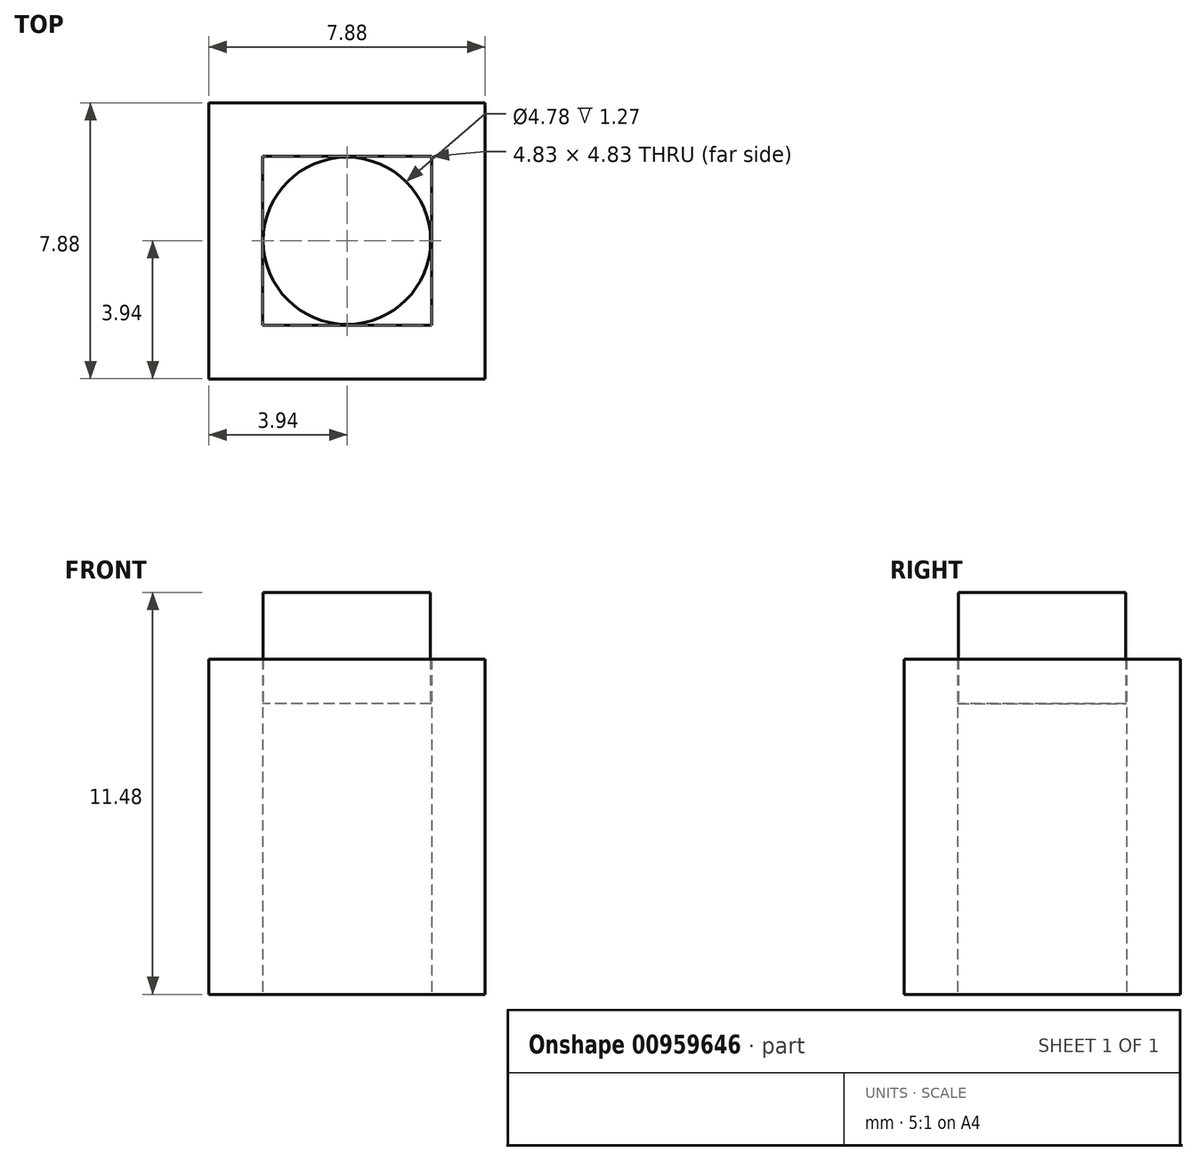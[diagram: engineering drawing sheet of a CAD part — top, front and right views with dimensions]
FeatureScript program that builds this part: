
annotation { "Feature Type Name" : "Feature", "Feature Type Description" : "" }
export const myFeature = defineFeature(function(context is Context, id is Id, definition is map)
    precondition{}
    {
        {
            var Q0;
            Q0=qCreatedBy(makeId("Top.planeOp"),FACE);
            var sketch = newSketch(context, id + "F0", { "sketchPlane" : qUnion([Q0])});
            skLineSegment(sketch, "E0.bottom", {"start": v(2.41, 2.41) * mm, "end": v(-2.41, 2.41) * mm});
            skLineSegment(sketch, "E0.top", {"start": v(2.41, -2.41) * mm, "end": v(-2.41, -2.41) * mm});
            skLineSegment(sketch, "E0.left", {"start": v(2.41, 2.41) * mm, "end": v(2.41, -2.41) * mm});
            skLineSegment(sketch, "E0.right", {"start": v(-2.41, 2.41) * mm, "end": v(-2.41, -2.41) * mm});
            skPoint(sketch, "E0.middle", {"position": v(0, 0) * mm});
            skLineSegment(sketch, "E1.bottom", {"start": v(3.94, 3.94) * mm, "end": v(-3.94, 3.94) * mm});
            skLineSegment(sketch, "E1.top", {"start": v(3.94, -3.94) * mm, "end": v(-3.94, -3.94) * mm});
            skLineSegment(sketch, "E1.left", {"start": v(3.94, 3.94) * mm, "end": v(3.94, -3.94) * mm});
            skLineSegment(sketch, "E1.right", {"start": v(-3.94, 3.94) * mm, "end": v(-3.94, -3.94) * mm});
            skCircle(sketch, "E2", {"center": v(0, 0) * mm, "radius": 2.39 * mm});
            skSolve(sketch);
        }
        {
            var Q0;
            Q0=makeQuery(id+"F0.imprint","IMPRINT",FACE,{"disambiguationData":[TD([[makeQuery(id+"F0.imprint","IMPRINT",EDGE,{"derivedFrom":sQuery(id+"F0.wireOp",EDGE,"E0.bottom")}),-1.0]])]});
            extrude(context, id + "F1", {"entities" : qUnion([Q0]), "depth" : 9.58 * mm, "offsetDistance" : 25.4 * mm});
        }
        {
            var Q0;
            Q0=makeQuery(id+"F0.imprint","IMPRINT",FACE,{"disambiguationData":[TD([[makeQuery(id+"F0.imprint","IMPRINT",EDGE,{"derivedFrom":sQuery(id+"F0.wireOp",EDGE,"E0.bottom")}),1.0]])]});
            extrude(context, id + "F2", {"entities" : qUnion([Q0]), "depth" : 9.58 * mm, "offsetDistance" : 25.4 * mm, "hasSecondDirection" : true, "secondDirectionOppositeDirection" : false, "secondDirectionDepth" : 8.3 * mm});
        }
        {
            var Q0;
            Q0=makeQuery(id+"F0.imprint","IMPRINT",FACE,{"disambiguationData":[TD([[makeQuery(id+"F0.imprint","IMPRINT",EDGE,{"derivedFrom":sQuery(id+"F0.wireOp",EDGE,"E2")}),1.0]])]});
            extrude(context, id + "F3", {"entities" : qUnion([Q0]), "depth" : 11.48 * mm, "offsetDistance" : 25.4 * mm, "hasSecondDirection" : true, "secondDirectionOppositeDirection" : false, "secondDirectionDepth" : 8.3 * mm});
        }
    });
